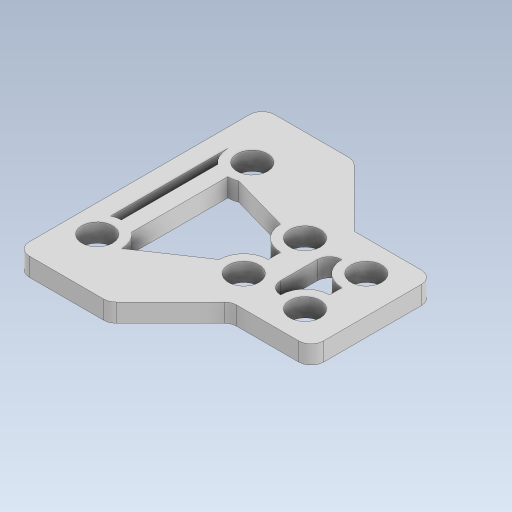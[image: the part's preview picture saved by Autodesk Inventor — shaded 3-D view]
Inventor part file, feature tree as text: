
AUTODESK INVENTOR PART (.ipt)
format: ipt  version: 2023.5 (Build 275446000, 446)  size: 421,888 bytes
history: native  units: mm
features: extrude x1, fillet x1, sketch x1
ambient origin geometry x8: Origin, YZ Plane, XZ Plane, XY Plane, X Axis, Y Axis, Z Axis, Center Point
bodies: Solid1 (feature_tree)
feature tree (3):
  extrude  "Extrusion1"  Depth=40.0mm
  fillet  "Fillet1"  Radius=5.0mm
  sketch  "Sketch1"  dims[d2=36.0mm d3=40.0mm d4=5.0mm d6=5.0mm d8=10.0mm d9=45.0deg d10=3.0mm d11=0.0mm d13=8.0mm d14=2.0mm d15=8.0mm d16=8.0mm d17=13.0mm d18=5.0mm d19=10.0mm d20=8.0mm d22=5.0mm d23=4.5mm d24=8.0mm]
